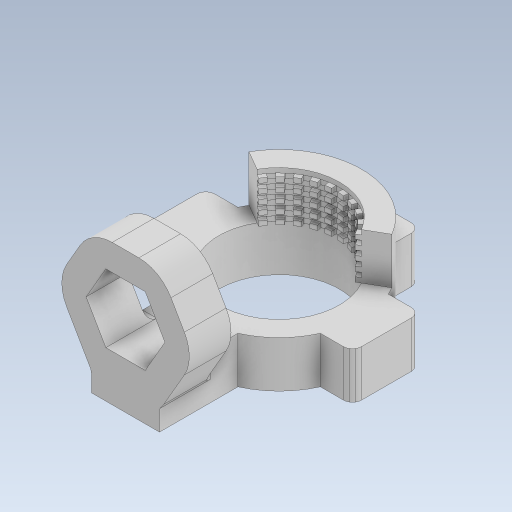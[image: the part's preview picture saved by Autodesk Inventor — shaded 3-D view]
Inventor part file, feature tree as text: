
AUTODESK INVENTOR PART (.ipt)
format: ipt  version: 2023 (Build 270158000, 158)  size: 1,107,968 bytes
history: native  units: in
note: dims shown in document units (in); Inventor stores cm internally (conversion verified against a paired STEP export)
features: sketch x6, extrude x5, projected_geometry x3, fillet x2, revolve x1
ambient origin geometry x8: Origin, YZ Plane, XZ Plane, XY Plane, X Axis, Y Axis, Z Axis, Center Point
bodies: Solid1 (feature_tree)
feature tree (17):
  extrude  "Extrusion1"  Depth=0.3937in TaperAngle=0.0deg
  extrude  "Extrusion2"  Depth=0.3937in TaperAngle=0.0deg
  extrude  "Extrusion3"  Depth=7.874in TaperAngle=120.0deg
  revolve  "Revolution1"  [1 undecoded]
  extrude  "Extrusion16"  Depth=0.3937in TaperAngle=0.0deg
  extrude  "Extrusion18"  Depth=0.0787in
  fillet  "Fillet6"  Radius=0.3543in
  fillet  "Fillet7"  Radius=0.315in
  sketch  "Sketch1"  dims[d0=1.0236in d1=0.3937in d2=0.0in]
  sketch  "Sketch2"  dims[d3=120.0deg d4=0.3937in d5=0.0in]
  sketch  "Sketch3"  dims[d6=0.0394in d7=7.874in d9=120.0deg]
  sketch  "Sketch4"  dims[d11=0.3937in d12=0.0in d14=3.937in d16=0.0394in d17=0.3937in d19=0.3937in]
  sketch  "Sketch29"  dims[d21=360.0deg d122=0.3937in d123=0.1969in d124=0.0in d125=0.0in]
  projected_geometry  "Projected Loop12"
  projected_geometry  "Projected Loop13"
  projected_geometry  "Projected Loop14"
  sketch  "Sketch32"  dims[d132=0.3346in d133=0.5906in d134=0.3543in d135=0.0in d136=0.315in d137=0.0787in d91=0.0344in d92=0.0344in d93=0.0197in d94=0.0344in d138=0.0in d139=0.0in d140=0.0in]
note: 1 required parameter value undecoded (feature->parameter linkage not recoverable at this tier; creation-order binding heuristic only, values carry confidence <= 0.55)
